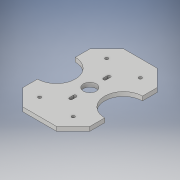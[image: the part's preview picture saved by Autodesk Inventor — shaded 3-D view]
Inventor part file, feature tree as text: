
AUTODESK INVENTOR PART (.ipt)
format: ipt  version: 2019 (Build 230136000, 136)  size: 176,640 bytes
history: native  units: in
note: dims shown in document units (in); Inventor stores cm internally (conversion verified against a paired STEP export)
features: extrude x5, sketch x5, chamfer x1
ambient origin geometry x8: Origin, YZ Plane, XZ Plane, XY Plane, X Axis, Y Axis, Z Axis, Center Point
bodies: Solid1 (feature_tree)
feature tree (11):
  extrude  "Extrusion1"  Depth=4.0in
  extrude  "Extrusion2"  Depth=6.0in
  extrude  "Extrusion3"  Depth=1.0in
  extrude  "Extrusion4"  Depth=1.0in
  chamfer  "Chamfer1"  Distance=1.0in
  extrude  "Extrusion5"  Depth=0.25in
  sketch  "Sketch1"  dims[d0=2.5in d7=4.0in]
  sketch  "Sketch2"  dims[d8=6.0in d9=1.0in]
  sketch  "Sketch3"  dims[d10=1.0in d11=1.0in]
  sketch  "Sketch4"  dims[d12=1.0in d13=1.0in]
  sketch  "Sketch5"  dims[d14=1.0in d15=1.0in d16=1.0in d17=0.1875in d18=0.1875in d19=0.1875in d20=0.1875in d21=0.25in d22=0.0in d23=0.7677in d24=0.25in d25=0.0in d26=0.25in d27=0.0in d28=2.5in d29=0.2362in d30=0.2362in d31=0.1875in d32=0.1875in d33=0.25in d34=0.0in d35=1.0in d36=0.125in d37=45.0deg d38=2.25in d39=2.25in d40=0.25in d41=0.0in]
